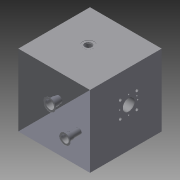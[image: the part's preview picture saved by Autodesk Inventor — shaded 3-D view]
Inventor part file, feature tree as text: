
AUTODESK INVENTOR PART (.ipt)
format: ipt  version: 2014 (Build 180170000, 170)  size: 369,664 bytes
history: native  units: mm
features: other x51, sketch x5, extrude x1
ambient origin geometry x8: Origin, YZ Plane, XZ Plane, XY Plane, X Axis, Y Axis, Z Axis, Center Point
bodies: 实体1 (feature_tree)
feature tree (57):
  extrude  "拉伸1"  TaperAngle=0.0deg  [1 undecoded]
  other  "UCS1"
  other  "UCS2"
  other  "UCS3"
  other  "UCS4"
  other  "UCS5"
  other  "UCS6"
  other  "iFeature4:2"
  other  "iFeature4:1"
  other  "删除面1"
  sketch  "草图1"  dims[d0=200.0mm d1=0.0mm]
  other  "UCS1: YZ 平面"
  other  "UCS1: XZ 平面"
  other  "UCS1: XY 平面"
  other  "UCS1: X 轴"
  other  "UCS1: Y 轴"
  other  "UCS1: Z 轴"
  other  "UCS1: 原点"
  other  "UCS2: YZ 平面"
  other  "UCS2: XZ 平面"
  other  "UCS2: XY 平面"
  other  "UCS2: X 轴"
  other  "UCS2: Y 轴"
  other  "UCS2: Z 轴"
  other  "UCS2: 原点"
  other  "UCS3: YZ 平面"
  other  "UCS3: XZ 平面"
  other  "UCS3: XY 平面"
  other  "UCS3: X 轴"
  other  "UCS3: Y 轴"
  other  "UCS3: Z 轴"
  other  "UCS3: 原点"
  other  "UCS4: YZ 平面"
  other  "UCS4: XZ 平面"
  other  "UCS4: XY 平面"
  other  "UCS4: X 轴"
  other  "UCS4: Y 轴"
  other  "UCS4: Z 轴"
  other  "UCS4: 原点"
  other  "UCS5: YZ 平面"
  other  "UCS5: XZ 平面"
  other  "UCS5: XY 平面"
  other  "UCS5: X 轴"
  other  "UCS5: Y 轴"
  other  "UCS5: Z 轴"
  other  "UCS5: 原点"
  other  "UCS6: YZ 平面"
  other  "UCS6: XZ 平面"
  other  "UCS6: XY 平面"
  other  "UCS6: X 轴"
  other  "UCS6: Y 轴"
  other  "UCS6: Z 轴"
  other  "UCS6: 原点"
  sketch  "草图4"  dims[d2=0.0mm d3=0.0mm d4=0.0mm d5=0.0mm d6=0.0mm d7=0.0mm]
  sketch  "草图6"  dims[d8=0.0mm d9=0.0mm d10=0.0mm d11=0.0mm d12=0.0mm d13=0.0mm]
  sketch  "草图7"  dims[d14=0.0mm d15=0.0mm d16=0.0mm d17=0.0mm d18=0.0mm d19=0.0mm]
  sketch  "草图8"  dims[d20=0.0mm d21=0.0mm d22=0.0mm d23=0.0mm d24=0.0mm d25=0.0mm d26=0.0mm d27=0.0mm d28=0.0mm d29=0.0mm d30=0.0mm d31=0.0mm d32=0.0mm d33=0.0mm d34=0.0mm d35=0.0mm d36=0.0mm d37=0.0mm d38=0.0mm d39=0.0mm d40=0.0mm d41=0.0mm d50=0.0mm d54=-17.0mm d55=0.0mm d59=-17.0mm d60=0.0mm d78=0.0mm d84=0.0mm d88=0.0mm]
note: 1 required parameter value undecoded (feature->parameter linkage not recoverable at this tier; creation-order binding heuristic only, values carry confidence <= 0.55)
